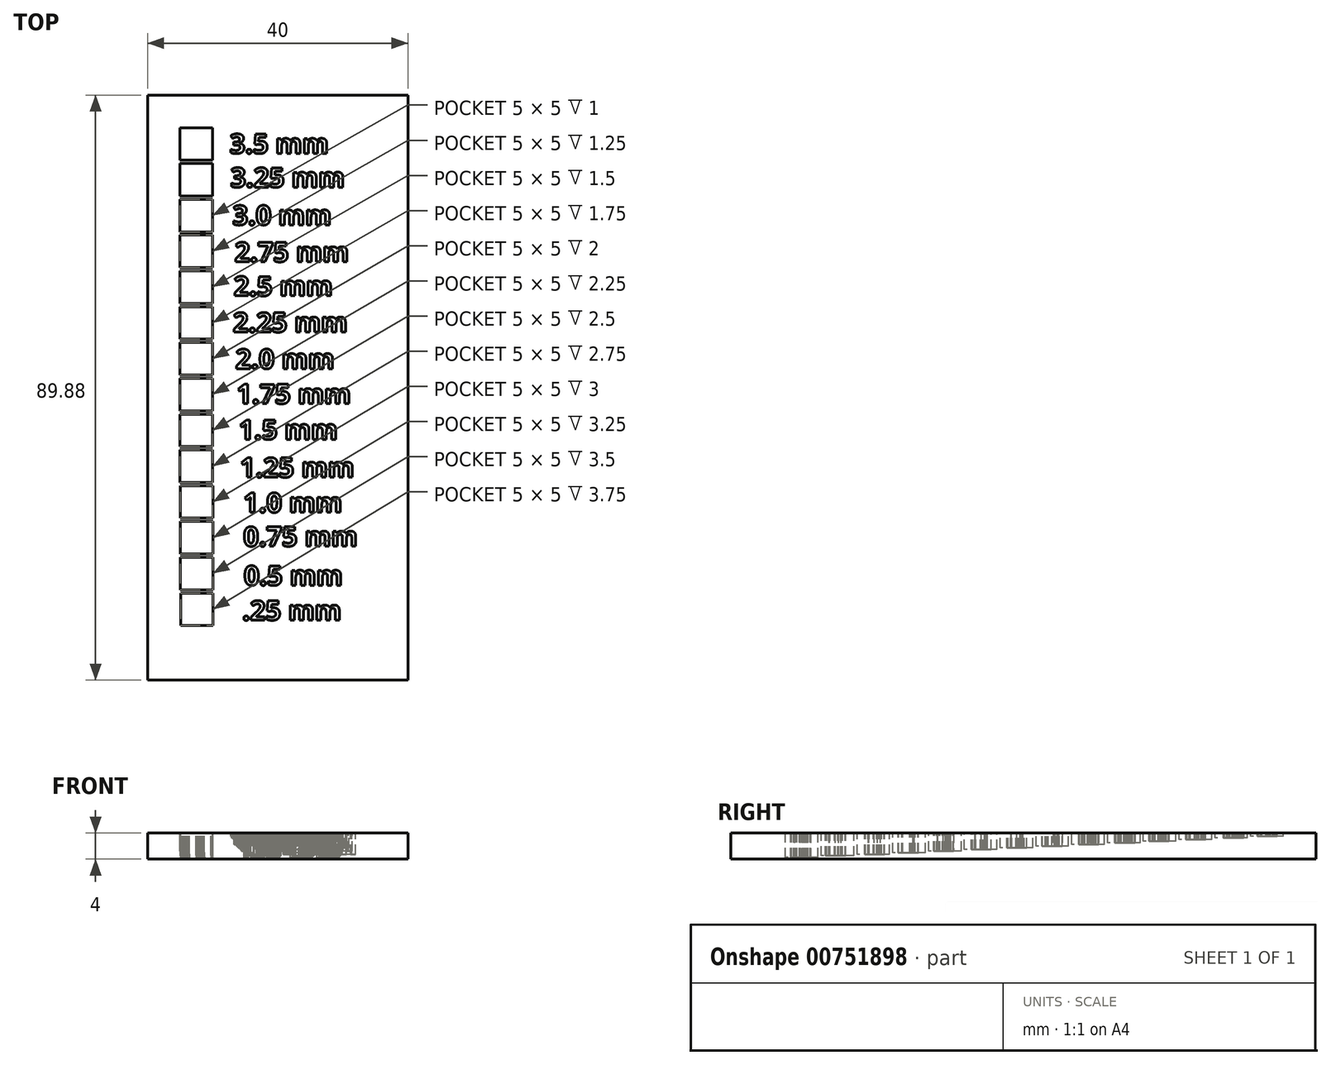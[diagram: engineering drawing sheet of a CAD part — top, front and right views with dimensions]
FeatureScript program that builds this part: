
annotation { "Feature Type Name" : "Feature", "Feature Type Description" : "" }
export const myFeature = defineFeature(function(context is Context, id is Id, definition is map)
    precondition{}
    {
        {
            var Q0;
            Q0=qCreatedBy(makeId("Top.planeOp"),FACE);
            var sketch = newSketch(context, id + "F0", { "sketchPlane" : qUnion([Q0])});
            skLineSegment(sketch, "E0.bottom", {"start": v(-50, 50) * mm, "end": v(-10, 50) * mm});
            skLineSegment(sketch, "E0.top", {"start": v(-50, -39.88) * mm, "end": v(-10, -39.88) * mm});
            skLineSegment(sketch, "E0.left", {"start": v(-50, 50) * mm, "end": v(-50, -39.88) * mm});
            skLineSegment(sketch, "E0.right", {"start": v(-10, 50) * mm, "end": v(-10, -39.88) * mm});
            skSolve(sketch);
        }
        {
            var Q0;
            Q0 = qSketchRegion(id + "F0", true);
            extrude(context, id + "F1", {"entities" : qUnion([Q0]), "depth" : 4 * mm, "offsetDistance" : 25 * mm});
        }
        {
            var Q0;
            Q0=makeQuery(id+"F1.opExtrude","CAP_FACE",FACE,{"disambiguationData":[OSD([sQuery(id+"F0.wireOp",EDGE,"E0.bottom"),sQuery(id+"F0.wireOp",EDGE,"E0.top"),sQuery(id+"F0.wireOp",EDGE,"E0.left"),sQuery(id+"F0.wireOp",EDGE,"E0.right")])],"isStart":false});
            var sketch = newSketch(context, id + "F2", { "sketchPlane" : qUnion([Q0])});
            skLineSegment(sketch, "E1.bottom", {"start": v(-45, 45) * mm, "end": v(-40, 45) * mm});
            skLineSegment(sketch, "E1.top", {"start": v(-45, 40) * mm, "end": v(-40, 40) * mm});
            skLineSegment(sketch, "E1.left", {"start": v(-45, 45) * mm, "end": v(-45, 40) * mm});
            skLineSegment(sketch, "E1.right", {"start": v(-40, 45) * mm, "end": v(-40, 40) * mm});
            skLineSegment(sketch, "E2.1.0.0", {"start": v(-40, 39.5) * mm, "end": v(-40, 34.5) * mm});
            skLineSegment(sketch, "E2.1.0.1", {"start": v(-45, 39.5) * mm, "end": v(-45, 34.5) * mm});
            skLineSegment(sketch, "E2.1.0.2", {"start": v(-45, 34.5) * mm, "end": v(-40, 34.5) * mm});
            skLineSegment(sketch, "E2.1.0.3", {"start": v(-45, 39.5) * mm, "end": v(-40, 39.5) * mm});
            skLineSegment(sketch, "E2.2.0.0", {"start": v(-40, 34) * mm, "end": v(-40, 29) * mm});
            skLineSegment(sketch, "E2.2.0.1", {"start": v(-45, 34) * mm, "end": v(-45, 29) * mm});
            skLineSegment(sketch, "E2.2.0.2", {"start": v(-45, 29) * mm, "end": v(-40, 29) * mm});
            skLineSegment(sketch, "E2.2.0.3", {"start": v(-45, 34) * mm, "end": v(-40, 34) * mm});
            skLineSegment(sketch, "E2.3.0.0", {"start": v(-40, 28.5) * mm, "end": v(-40, 23.5) * mm});
            skLineSegment(sketch, "E2.3.0.1", {"start": v(-45, 28.5) * mm, "end": v(-45, 23.5) * mm});
            skLineSegment(sketch, "E2.3.0.2", {"start": v(-45, 23.5) * mm, "end": v(-40, 23.5) * mm});
            skLineSegment(sketch, "E2.3.0.3", {"start": v(-45, 28.5) * mm, "end": v(-40, 28.5) * mm});
            skLineSegment(sketch, "E2.4.0.0", {"start": v(-40, 23) * mm, "end": v(-40, 18) * mm});
            skLineSegment(sketch, "E2.4.0.1", {"start": v(-45, 23) * mm, "end": v(-45, 18) * mm});
            skLineSegment(sketch, "E2.4.0.2", {"start": v(-45, 18) * mm, "end": v(-40, 18) * mm});
            skLineSegment(sketch, "E2.4.0.3", {"start": v(-45, 23) * mm, "end": v(-40, 23) * mm});
            skLineSegment(sketch, "E2.5.0.0", {"start": v(-40, 17.5) * mm, "end": v(-40, 12.5) * mm});
            skLineSegment(sketch, "E2.5.0.1", {"start": v(-45, 17.5) * mm, "end": v(-45, 12.5) * mm});
            skLineSegment(sketch, "E2.5.0.2", {"start": v(-45, 12.5) * mm, "end": v(-40, 12.5) * mm});
            skLineSegment(sketch, "E2.5.0.3", {"start": v(-45, 17.5) * mm, "end": v(-40, 17.5) * mm});
            skLineSegment(sketch, "E2.6.0.0", {"start": v(-40, 12) * mm, "end": v(-40, 7) * mm});
            skLineSegment(sketch, "E2.6.0.1", {"start": v(-45, 12) * mm, "end": v(-45, 7) * mm});
            skLineSegment(sketch, "E2.6.0.2", {"start": v(-45, 7) * mm, "end": v(-40, 7) * mm});
            skLineSegment(sketch, "E2.6.0.3", {"start": v(-45, 12) * mm, "end": v(-40, 12) * mm});
            skLineSegment(sketch, "E2.7.0.0", {"start": v(-40, 6.5) * mm, "end": v(-40, 1.5) * mm});
            skLineSegment(sketch, "E2.7.0.1", {"start": v(-45, 6.5) * mm, "end": v(-45, 1.5) * mm});
            skLineSegment(sketch, "E2.7.0.2", {"start": v(-45, 1.5) * mm, "end": v(-40, 1.5) * mm});
            skLineSegment(sketch, "E2.7.0.3", {"start": v(-45, 6.5) * mm, "end": v(-40, 6.5) * mm});
            skLineSegment(sketch, "E2.8.0.0", {"start": v(-40, 1) * mm, "end": v(-40, -4) * mm});
            skLineSegment(sketch, "E2.8.0.1", {"start": v(-45, 1) * mm, "end": v(-45, -4) * mm});
            skLineSegment(sketch, "E2.8.0.2", {"start": v(-45, -4) * mm, "end": v(-40, -4) * mm});
            skLineSegment(sketch, "E2.8.0.3", {"start": v(-45, 1) * mm, "end": v(-40, 1) * mm});
            skLineSegment(sketch, "E2.9.0.0", {"start": v(-40, -4.5) * mm, "end": v(-40, -9.5) * mm});
            skLineSegment(sketch, "E2.9.0.1", {"start": v(-45, -4.5) * mm, "end": v(-45, -9.5) * mm});
            skLineSegment(sketch, "E2.9.0.2", {"start": v(-45, -9.5) * mm, "end": v(-40, -9.5) * mm});
            skLineSegment(sketch, "E2.9.0.3", {"start": v(-45, -4.5) * mm, "end": v(-40, -4.5) * mm});
            skLineSegment(sketch, "E2.direction1", {"start": v(-45, 40) * mm, "end": v(-45, 34.5) * mm, "construction": true});
            skLineSegment(sketch, "E3.1.0.0", {"start": v(-44.98, -15) * mm, "end": v(-39.98, -15) * mm});
            skLineSegment(sketch, "E3.1.0.1", {"start": v(-39.98, -10) * mm, "end": v(-39.98, -15) * mm});
            skLineSegment(sketch, "E3.1.0.2", {"start": v(-44.98, -10) * mm, "end": v(-39.98, -10) * mm});
            skLineSegment(sketch, "E3.1.0.3", {"start": v(-44.98, -10) * mm, "end": v(-44.98, -15) * mm});
            skLineSegment(sketch, "E3.2.0.0", {"start": v(-44.96, -20.5) * mm, "end": v(-39.96, -20.5) * mm});
            skLineSegment(sketch, "E3.2.0.1", {"start": v(-39.96, -15.5) * mm, "end": v(-39.96, -20.5) * mm});
            skLineSegment(sketch, "E3.2.0.2", {"start": v(-44.96, -15.5) * mm, "end": v(-39.96, -15.5) * mm});
            skLineSegment(sketch, "E3.2.0.3", {"start": v(-44.96, -15.5) * mm, "end": v(-44.96, -20.5) * mm});
            skLineSegment(sketch, "E3.3.0.0", {"start": v(-44.94, -26) * mm, "end": v(-39.94, -26) * mm});
            skLineSegment(sketch, "E3.3.0.1", {"start": v(-39.94, -21) * mm, "end": v(-39.94, -26) * mm});
            skLineSegment(sketch, "E3.3.0.2", {"start": v(-44.94, -21) * mm, "end": v(-39.94, -21) * mm});
            skLineSegment(sketch, "E3.3.0.3", {"start": v(-44.94, -21) * mm, "end": v(-44.94, -26) * mm});
            skLineSegment(sketch, "E3.4.0.0", {"start": v(-44.92, -31.5) * mm, "end": v(-39.92, -31.5) * mm});
            skLineSegment(sketch, "E3.4.0.1", {"start": v(-39.92, -26.5) * mm, "end": v(-39.92, -31.5) * mm});
            skLineSegment(sketch, "E3.4.0.2", {"start": v(-44.92, -26.5) * mm, "end": v(-39.92, -26.5) * mm});
            skLineSegment(sketch, "E3.4.0.3", {"start": v(-44.92, -26.5) * mm, "end": v(-44.92, -31.5) * mm});
            skLineSegment(sketch, "E3.direction1", {"start": v(-45, -9.5) * mm, "end": v(-44.98, -15) * mm, "construction": true});
            skSolve(sketch);
        }
        {
            var Q0;
            Q0=makeQuery(id+"F2.imprint","IMPRINT",FACE,{"disambiguationData":[TD([[makeQuery(id+"F2.imprint","IMPRINT",EDGE,{"derivedFrom":sQuery(id+"F2.wireOp",EDGE,"E1.bottom")}),1.0]])]});
            var sketch = newSketch(context, id + "F3", { "sketchPlane" : qUnion([Q0])});
            skText(sketch, "E4", { "text": "3.5 mm", "fontName": "OpenSans-Bold.ttf"});
            const initialGuessF3  = {"E4": [-0.03737, 0.04105, 1, 0, 0.003]};
            skSetInitialGuess(sketch, initialGuessF3);
            skSolve(sketch);
        }
        {
            var Q0;
            Q0 = qSketchRegion(id + "F3", true);
            extrude(context, id + "F4", {"entities" : qUnion([Q0]), "operationType" : NewBodyOperationType.REMOVE, "oppositeDirection" : true, "depth" : 0.5 * mm, "offsetDistance" : 25 * mm});
        }
        {
            var Q0;
            Q0=makeQuery(id+"F2.imprint","IMPRINT",FACE,{"disambiguationData":[TD([[makeQuery(id+"F2.imprint","IMPRINT",EDGE,{"derivedFrom":sQuery(id+"F2.wireOp",EDGE,"E1.bottom")}),-1.0]])]});
            extrude(context, id + "F5", {"entities" : qUnion([Q0]), "operationType" : NewBodyOperationType.REMOVE, "oppositeDirection" : true, "depth" : 0.5 * mm, "offsetDistance" : 25 * mm});
        }
        {
            var Q0;
            Q0=makeQuery(id+"F1.opExtrude","CAP_FACE",FACE,{"disambiguationData":[OSD([sQuery(id+"F0.wireOp",EDGE,"E0.bottom"),sQuery(id+"F0.wireOp",EDGE,"E0.top"),sQuery(id+"F0.wireOp",EDGE,"E0.left"),sQuery(id+"F0.wireOp",EDGE,"E0.right")])],"isStart":false});
            var sketch = newSketch(context, id + "F6", { "sketchPlane" : qUnion([Q0])});
            skText(sketch, "E5", { "text": "3.25 mm", "fontName": "OpenSans-Bold.ttf"});
            const initialGuessF6  = {"E5": [-0.03727, 0.03586, 1, 0, 0.003]};
            skSetInitialGuess(sketch, initialGuessF6);
            skSolve(sketch);
        }
        {
            var Q0;
            Q0 = qSketchRegion(id + "F6", true);
            extrude(context, id + "F7", {"entities" : qUnion([Q0]), "operationType" : NewBodyOperationType.REMOVE, "oppositeDirection" : true, "depth" : 0.75 * mm, "offsetDistance" : 25 * mm});
        }
        {
            var Q0;
            Q0=makeQuery(id+"F2.imprint","IMPRINT",FACE,{"disambiguationData":[TD([[makeQuery(id+"F2.imprint","IMPRINT",EDGE,{"derivedFrom":sQuery(id+"F2.wireOp",EDGE,"E2.1.0.0")}),-1.0]])]});
            extrude(context, id + "F8", {"entities" : qUnion([Q0]), "operationType" : NewBodyOperationType.REMOVE, "oppositeDirection" : true, "depth" : 0.75 * mm, "offsetDistance" : 25 * mm});
        }
        {
            var Q0;
            Q0=makeQuery(id+"F2.imprint","IMPRINT",FACE,{"disambiguationData":[TD([[makeQuery(id+"F2.imprint","IMPRINT",EDGE,{"derivedFrom":sQuery(id+"F2.wireOp",EDGE,"E1.bottom")}),1.0]])]});
            var sketch = newSketch(context, id + "F9", { "sketchPlane" : qUnion([Q0])});
            skText(sketch, "E6", { "text": "3.0 mm", "fontName": "OpenSans-Bold.ttf"});
            const initialGuessF9  = {"E6": [-0.03694, 0.03006, 1, 0, 0.003]};
            skSetInitialGuess(sketch, initialGuessF9);
            skSolve(sketch);
        }
        {
            var Q0;
            Q0 = qSketchRegion(id + "F9", true);
            extrude(context, id + "F10", {"entities" : qUnion([Q0]), "operationType" : NewBodyOperationType.REMOVE, "oppositeDirection" : true, "depth" : 1 * mm, "offsetDistance" : 25 * mm});
        }
        {
            var Q0;
            Q0=makeQuery(id+"F2.imprint","IMPRINT",FACE,{"disambiguationData":[TD([[makeQuery(id+"F2.imprint","IMPRINT",EDGE,{"derivedFrom":sQuery(id+"F2.wireOp",EDGE,"E2.2.0.0")}),-1.0]])]});
            extrude(context, id + "F11", {"entities" : qUnion([Q0]), "operationType" : NewBodyOperationType.REMOVE, "oppositeDirection" : true, "depth" : 1 * mm, "offsetDistance" : 25 * mm});
        }
        {
            var Q0;
            Q0=makeQuery(id+"F2.imprint","IMPRINT",FACE,{"disambiguationData":[TD([[makeQuery(id+"F2.imprint","IMPRINT",EDGE,{"derivedFrom":sQuery(id+"F2.wireOp",EDGE,"E1.bottom")}),1.0]])]});
            var sketch = newSketch(context, id + "F12", { "sketchPlane" : qUnion([Q0])});
            skText(sketch, "E7", { "text": "2.75 mm", "fontName": "OpenSans-Bold.ttf"});
            const initialGuessF12  = {"E7": [-0.03663, 0.0244, 1, 0, 0.003]};
            skSetInitialGuess(sketch, initialGuessF12);
            skSolve(sketch);
        }
        {
            var Q0;
            Q0 = qSketchRegion(id + "F12", true);
            extrude(context, id + "F13", {"entities" : qUnion([Q0]), "operationType" : NewBodyOperationType.REMOVE, "oppositeDirection" : true, "depth" : 1.25 * mm, "offsetDistance" : 25 * mm});
        }
        {
            var Q0;
            Q0=makeQuery(id+"F3.imprint","IMPRINT",FACE,{"disambiguationData":[TD([[makeQuery(id+"F3.imprint","IMPRINT",EDGE,{"derivedFrom":makeQuery(id+"F2.imprint","IMPRINT",EDGE,{"derivedFrom":sQuery(id+"F2.wireOp",EDGE,"E2.3.0.0")})}),-1.0]])]});
            extrude(context, id + "F14", {"entities" : qUnion([Q0]), "operationType" : NewBodyOperationType.REMOVE, "oppositeDirection" : true, "depth" : 1.25 * mm, "offsetDistance" : 25 * mm});
        }
        {
            var Q0;
            Q0=makeQuery(id+"F2.imprint","IMPRINT",FACE,{"disambiguationData":[TD([[makeQuery(id+"F2.imprint","IMPRINT",EDGE,{"derivedFrom":sQuery(id+"F2.wireOp",EDGE,"E1.bottom")}),1.0]])]});
            var sketch = newSketch(context, id + "F15", { "sketchPlane" : qUnion([Q0])});
            skText(sketch, "E8", { "text": "2.5 mm", "fontName": "OpenSans-Bold.ttf"});
            const initialGuessF15  = {"E8": [-0.03677, 0.01917, 1, 0, 0.003]};
            skSetInitialGuess(sketch, initialGuessF15);
            skSolve(sketch);
        }
        {
            var Q0;
            Q0 = qSketchRegion(id + "F15", true);
            extrude(context, id + "F16", {"entities" : qUnion([Q0]), "operationType" : NewBodyOperationType.REMOVE, "oppositeDirection" : true, "depth" : 1.5 * mm, "offsetDistance" : 25 * mm});
        }
        {
            var Q0;
            Q0=makeQuery(id+"F2.imprint","IMPRINT",FACE,{"disambiguationData":[TD([[makeQuery(id+"F2.imprint","IMPRINT",EDGE,{"derivedFrom":sQuery(id+"F2.wireOp",EDGE,"E2.4.0.0")}),-1.0]])]});
            extrude(context, id + "F17", {"entities" : qUnion([Q0]), "operationType" : NewBodyOperationType.REMOVE, "oppositeDirection" : true, "depth" : 1.5 * mm, "offsetDistance" : 25 * mm});
        }
        {
            var Q0;
            Q0=makeQuery(id+"F2.imprint","IMPRINT",FACE,{"disambiguationData":[TD([[makeQuery(id+"F2.imprint","IMPRINT",EDGE,{"derivedFrom":sQuery(id+"F2.wireOp",EDGE,"E1.bottom")}),1.0]])]});
            var sketch = newSketch(context, id + "F18", { "sketchPlane" : qUnion([Q0])});
            skText(sketch, "E9", { "text": "2.25 mm", "fontName": "OpenSans-Bold.ttf"});
            const initialGuessF18  = {"E9": [-0.03687, 0.0136, 1, 0, 0.003]};
            skSetInitialGuess(sketch, initialGuessF18);
            skSolve(sketch);
        }
        {
            var Q0;
            Q0 = qSketchRegion(id + "F18", true);
            extrude(context, id + "F19", {"entities" : qUnion([Q0]), "operationType" : NewBodyOperationType.REMOVE, "oppositeDirection" : true, "depth" : 1.75 * mm, "offsetDistance" : 25 * mm});
        }
        {
            var Q0;
            Q0=makeQuery(id+"F2.imprint","IMPRINT",FACE,{"disambiguationData":[TD([[makeQuery(id+"F2.imprint","IMPRINT",EDGE,{"derivedFrom":sQuery(id+"F2.wireOp",EDGE,"E2.5.0.0")}),-1.0]])]});
            extrude(context, id + "F20", {"entities" : qUnion([Q0]), "operationType" : NewBodyOperationType.REMOVE, "oppositeDirection" : true, "depth" : 1.75 * mm, "offsetDistance" : 25 * mm});
        }
        {
            var Q0;
            Q0=makeQuery(id+"F2.imprint","IMPRINT",FACE,{"disambiguationData":[TD([[makeQuery(id+"F2.imprint","IMPRINT",EDGE,{"derivedFrom":sQuery(id+"F2.wireOp",EDGE,"E1.bottom")}),1.0]])]});
            var sketch = newSketch(context, id + "F21", { "sketchPlane" : qUnion([Q0])});
            skText(sketch, "E10", { "text": "2.0 mm", "fontName": "OpenSans-Bold.ttf"});
            const initialGuessF21  = {"E10": [-0.03647, 0.00798, 1, 0, 0.003]};
            skSetInitialGuess(sketch, initialGuessF21);
            skSolve(sketch);
        }
        {
            var Q0;
            Q0 = qSketchRegion(id + "F21", true);
            var Q1;
            Q1=makeQuery(id+"F2.imprint","IMPRINT",FACE,{"disambiguationData":[TD([[makeQuery(id+"F2.imprint","IMPRINT",EDGE,{"derivedFrom":sQuery(id+"F2.wireOp",EDGE,"E2.6.0.0")}),-1.0]])]});
            extrude(context, id + "F22", {"entities" : qUnion([Q0, Q1]), "operationType" : NewBodyOperationType.REMOVE, "oppositeDirection" : true, "depth" : 2 * mm, "offsetDistance" : 25 * mm});
        }
        {
            var Q0;
            Q0=makeQuery(id+"F2.imprint","IMPRINT",FACE,{"disambiguationData":[TD([[makeQuery(id+"F2.imprint","IMPRINT",EDGE,{"derivedFrom":sQuery(id+"F2.wireOp",EDGE,"E1.bottom")}),1.0]])]});
            var sketch = newSketch(context, id + "F23", { "sketchPlane" : qUnion([Q0])});
            skText(sketch, "E11", { "text": "1.75 mm", "fontName": "OpenSans-Bold.ttf"});
            const initialGuessF23  = {"E11": [-0.03635, 0.0026, 1, 0, 0.003]};
            skSetInitialGuess(sketch, initialGuessF23);
            skSolve(sketch);
        }
        {
            var Q0;
            Q0 = qSketchRegion(id + "F23", true);
            var Q1;
            Q1=makeQuery(id+"F2.imprint","IMPRINT",FACE,{"disambiguationData":[TD([[makeQuery(id+"F2.imprint","IMPRINT",EDGE,{"derivedFrom":sQuery(id+"F2.wireOp",EDGE,"E2.7.0.0")}),-1.0]])]});
            extrude(context, id + "F24", {"entities" : qUnion([Q0, Q1]), "operationType" : NewBodyOperationType.REMOVE, "oppositeDirection" : true, "depth" : 2.25 * mm, "offsetDistance" : 25 * mm});
        }
        {
            var Q0;
            Q0=makeQuery(id+"F2.imprint","IMPRINT",FACE,{"disambiguationData":[TD([[makeQuery(id+"F2.imprint","IMPRINT",EDGE,{"derivedFrom":sQuery(id+"F2.wireOp",EDGE,"E1.bottom")}),1.0]])]});
            var sketch = newSketch(context, id + "F25", { "sketchPlane" : qUnion([Q0])});
            skText(sketch, "E12", { "text": "1.5 mm", "fontName": "OpenSans-Bold.ttf"});
            const initialGuessF25  = {"E12": [-0.036, -0.00288, 1, 0, 0.003]};
            skSetInitialGuess(sketch, initialGuessF25);
            skSolve(sketch);
        }
        {
            var Q0;
            Q0 = qSketchRegion(id + "F25", true);
            var Q1;
            Q1=makeQuery(id+"F2.imprint","IMPRINT",FACE,{"disambiguationData":[TD([[makeQuery(id+"F2.imprint","IMPRINT",EDGE,{"derivedFrom":sQuery(id+"F2.wireOp",EDGE,"E2.8.0.0")}),-1.0]])]});
            extrude(context, id + "F26", {"entities" : qUnion([Q0, Q1]), "operationType" : NewBodyOperationType.REMOVE, "oppositeDirection" : true, "depth" : 2.5 * mm, "offsetDistance" : 25 * mm});
        }
        {
            var Q0;
            Q0=makeQuery(id+"F2.imprint","IMPRINT",FACE,{"disambiguationData":[TD([[makeQuery(id+"F2.imprint","IMPRINT",EDGE,{"derivedFrom":sQuery(id+"F2.wireOp",EDGE,"E1.bottom")}),1.0]])]});
            var sketch = newSketch(context, id + "F27", { "sketchPlane" : qUnion([Q0])});
            skText(sketch, "E13", { "text": "1.25 mm", "fontName": "OpenSans-Bold.ttf"});
            const initialGuessF27  = {"E13": [-0.0358, -0.0087, 1, 0, 0.003]};
            skSetInitialGuess(sketch, initialGuessF27);
            skSolve(sketch);
        }
        {
            var Q0;
            Q0 = qSketchRegion(id + "F27", true);
            var Q1;
            Q1=makeQuery(id+"F2.imprint","IMPRINT",FACE,{"disambiguationData":[TD([[makeQuery(id+"F2.imprint","IMPRINT",EDGE,{"derivedFrom":sQuery(id+"F2.wireOp",EDGE,"E2.9.0.0")}),-1.0]])]});
            extrude(context, id + "F28", {"entities" : qUnion([Q0, Q1]), "operationType" : NewBodyOperationType.REMOVE, "oppositeDirection" : true, "depth" : 2.75 * mm, "offsetDistance" : 25 * mm});
        }
        {
            var Q0;
            Q0=makeQuery(id+"F2.imprint","IMPRINT",FACE,{"disambiguationData":[TD([[makeQuery(id+"F2.imprint","IMPRINT",EDGE,{"derivedFrom":sQuery(id+"F2.wireOp",EDGE,"E1.bottom")}),1.0]])]});
            var sketch = newSketch(context, id + "F29", { "sketchPlane" : qUnion([Q0])});
            skText(sketch, "E14", { "text": "1.0 mm", "fontName": "OpenSans-Bold.ttf"});
            const initialGuessF29  = {"E14": [-0.0353, -0.0141, 1, 0, 0.003]};
            skSetInitialGuess(sketch, initialGuessF29);
            skSolve(sketch);
        }
        {
            var Q0;
            Q0 = qSketchRegion(id + "F29", true);
            var Q1;
            Q1=makeQuery(id+"F2.imprint","IMPRINT",FACE,{"disambiguationData":[TD([[makeQuery(id+"F2.imprint","IMPRINT",EDGE,{"derivedFrom":sQuery(id+"F2.wireOp",EDGE,"E3.1.0.0")}),1.0]])]});
            extrude(context, id + "F30", {"entities" : qUnion([Q0, Q1]), "operationType" : NewBodyOperationType.REMOVE, "oppositeDirection" : true, "depth" : 3 * mm, "offsetDistance" : 25 * mm});
        }
        {
            var Q0;
            Q0=makeQuery(id+"F2.imprint","IMPRINT",FACE,{"disambiguationData":[TD([[makeQuery(id+"F2.imprint","IMPRINT",EDGE,{"derivedFrom":sQuery(id+"F2.wireOp",EDGE,"E1.bottom")}),1.0]])]});
            var sketch = newSketch(context, id + "F31", { "sketchPlane" : qUnion([Q0])});
            skText(sketch, "E15", { "text": "0.75 mm", "fontName": "OpenSans-Bold.ttf"});
            const initialGuessF31  = {"E15": [-0.03529, -0.0193, 1, 0, 0.003]};
            skSetInitialGuess(sketch, initialGuessF31);
            skSolve(sketch);
        }
        {
            var Q0;
            Q0 = qSketchRegion(id + "F31", true);
            var Q1;
            Q1=makeQuery(id+"F2.imprint","IMPRINT",FACE,{"disambiguationData":[TD([[makeQuery(id+"F2.imprint","IMPRINT",EDGE,{"derivedFrom":sQuery(id+"F2.wireOp",EDGE,"E3.2.0.0")}),1.0]])]});
            extrude(context, id + "F32", {"entities" : qUnion([Q0, Q1]), "operationType" : NewBodyOperationType.REMOVE, "oppositeDirection" : true, "depth" : 3.25 * mm, "offsetDistance" : 25 * mm});
        }
        {
            var Q0;
            Q0=makeQuery(id+"F2.imprint","IMPRINT",FACE,{"disambiguationData":[TD([[makeQuery(id+"F2.imprint","IMPRINT",EDGE,{"derivedFrom":sQuery(id+"F2.wireOp",EDGE,"E1.bottom")}),1.0]])]});
            var sketch = newSketch(context, id + "F33", { "sketchPlane" : qUnion([Q0])});
            skText(sketch, "E16", { "text": "0.5 mm", "fontName": "OpenSans-Bold.ttf"});
            const initialGuessF33  = {"E16": [-0.0352, -0.0253, 1, 0, 0.003]};
            skSetInitialGuess(sketch, initialGuessF33);
            skSolve(sketch);
        }
        {
            var Q0;
            Q0 = qSketchRegion(id + "F33", true);
            var Q1;
            Q1=makeQuery(id+"F2.imprint","IMPRINT",FACE,{"disambiguationData":[TD([[makeQuery(id+"F2.imprint","IMPRINT",EDGE,{"derivedFrom":sQuery(id+"F2.wireOp",EDGE,"E3.3.0.0")}),1.0]])]});
            extrude(context, id + "F34", {"entities" : qUnion([Q0, Q1]), "operationType" : NewBodyOperationType.REMOVE, "oppositeDirection" : true, "depth" : 3.5 * mm, "offsetDistance" : 25 * mm});
        }
        {
            var Q0;
            Q0=makeQuery(id+"F2.imprint","IMPRINT",FACE,{"disambiguationData":[TD([[makeQuery(id+"F2.imprint","IMPRINT",EDGE,{"derivedFrom":sQuery(id+"F2.wireOp",EDGE,"E1.bottom")}),1.0]])]});
            var sketch = newSketch(context, id + "F35", { "sketchPlane" : qUnion([Q0])});
            skText(sketch, "E17", { "text": ".25 mm", "fontName": "OpenSans-Bold.ttf"});
            const initialGuessF35  = {"E17": [-0.03544, -0.03066, 1, 0, 0.003]};
            skSetInitialGuess(sketch, initialGuessF35);
            skSolve(sketch);
        }
        {
            var Q0;
            Q0 = qSketchRegion(id + "F35", true);
            var Q1;
            Q1=makeQuery(id+"F2.imprint","IMPRINT",FACE,{"disambiguationData":[TD([[makeQuery(id+"F2.imprint","IMPRINT",EDGE,{"derivedFrom":sQuery(id+"F2.wireOp",EDGE,"E3.4.0.0")}),1.0]])]});
            extrude(context, id + "F36", {"entities" : qUnion([Q0, Q1]), "operationType" : NewBodyOperationType.REMOVE, "oppositeDirection" : true, "depth" : 3.75 * mm, "offsetDistance" : 25 * mm});
        }
    });
